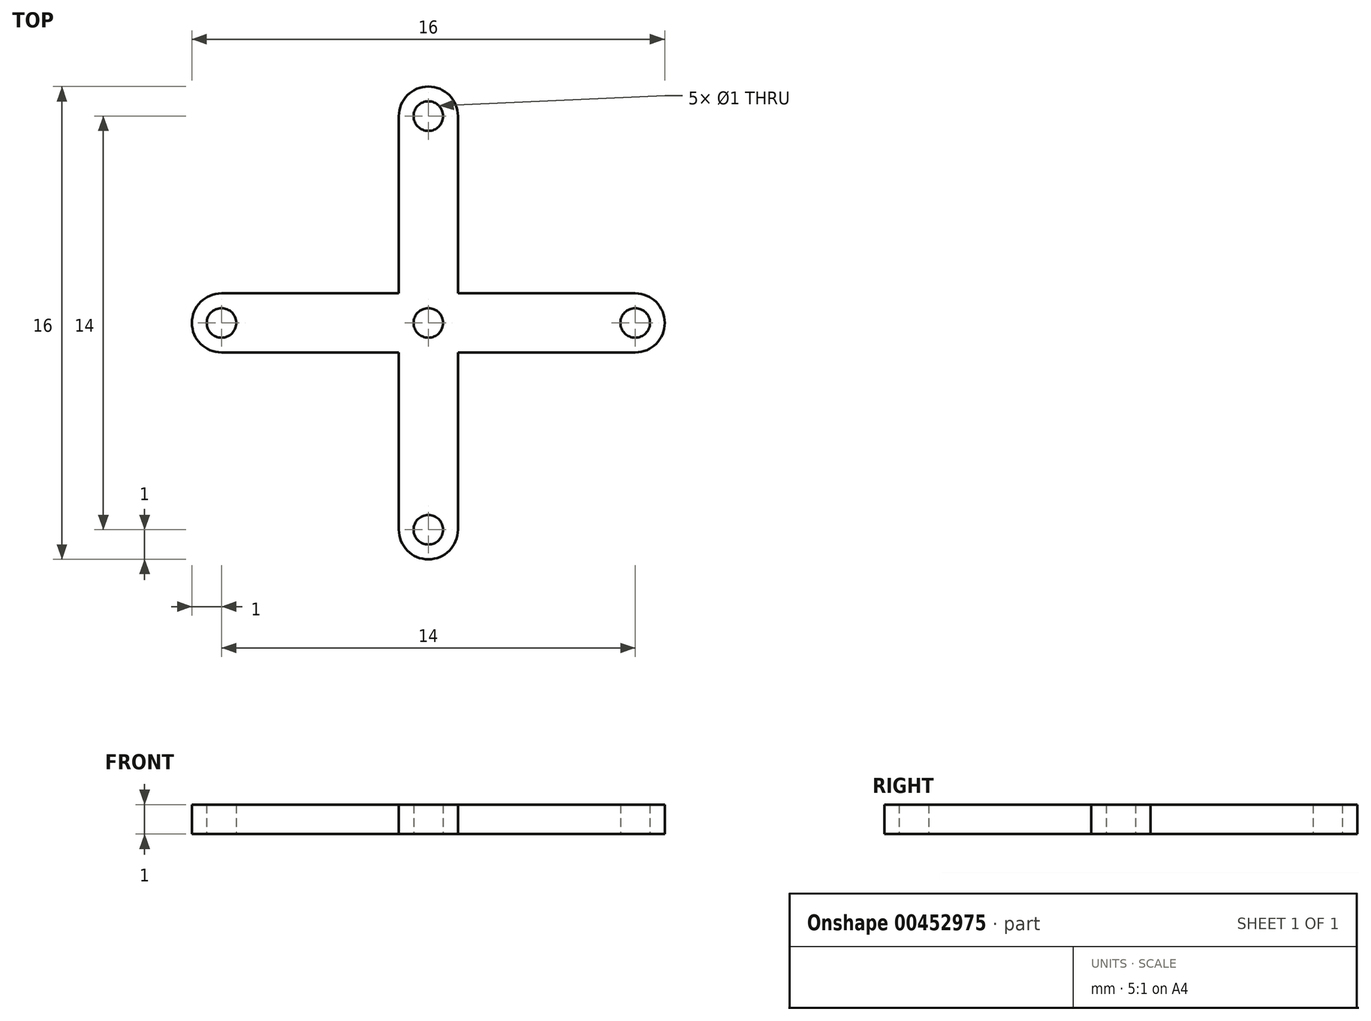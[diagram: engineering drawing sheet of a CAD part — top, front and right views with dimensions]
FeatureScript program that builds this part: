
annotation { "Feature Type Name" : "Feature", "Feature Type Description" : "" }
export const myFeature = defineFeature(function(context is Context, id is Id, definition is map)
    precondition{}
    {
        {
            var Q0;
            Q0=qCreatedBy(makeId("Top.planeOp"),FACE);
            var sketch = newSketch(context, id + "F0", { "sketchPlane" : qUnion([Q0])});
            skCircle(sketch, "E0", {"center": v(0, 7) * mm, "radius": 0.5 * mm});
            skCircle(sketch, "E1", {"center": v(0, 7) * mm, "radius": 1 * mm});
            skCircle(sketch, "E2.1.0", {"center": v(-7, 0) * mm, "radius": 0.5 * mm});
            skCircle(sketch, "E2.1.1", {"center": v(-7, 0) * mm, "radius": 1 * mm});
            skCircle(sketch, "E2.2.0", {"center": v(0, -7) * mm, "radius": 0.5 * mm});
            skCircle(sketch, "E2.2.1", {"center": v(0, -7) * mm, "radius": 1 * mm});
            skCircle(sketch, "E2.3.0", {"center": v(7, 0) * mm, "radius": 0.5 * mm});
            skCircle(sketch, "E2.3.1", {"center": v(7, 0) * mm, "radius": 1 * mm});
            skPoint(sketch, "E2.center", {"position": v(0, 0) * mm});
            skLineSegment(sketch, "E3", {"start": v(-1, 7) * mm, "end": v(-1, -7) * mm});
            skLineSegment(sketch, "E4.MirrorCS", {"start": v(1, 7) * mm, "end": v(1, -7) * mm});
            skLineSegment(sketch, "E5", {"start": v(-7, 1) * mm, "end": v(7, 1) * mm});
            skLineSegment(sketch, "E6.MirrorCS", {"start": v(-7, -1) * mm, "end": v(7, -1) * mm});
            skCircle(sketch, "E7", {"center": v(0, 0) * mm, "radius": 0.5 * mm});
            skSolve(sketch);
        }
        {
            var Q0;
            {var subQ0=sQuery(id+"F0.wireOp",EDGE,"E3");var subQ1=sQuery(id+"F0.wireOp",EDGE,"E1");var subQ2=makeQuery(id+"F0.imprint","INTERSECT",VERTEX,{"derivedFrom":[subQ1,subQ0]});Q0=makeQuery(id+"F0.imprint","IMPRINT",FACE,{"disambiguationData":[TD([[makeQuery(id+"F0.imprint","IMPRINT",EDGE,{"disambiguationData":[TD([[subQ2,-1.0]])],"derivedFrom":subQ1}),-1.0]])]});}
            var Q1;
            Q1=makeQuery(id+"F0.imprint","IMPRINT",FACE,{"disambiguationData":[TD([[makeQuery(id+"F0.imprint","IMPRINT",EDGE,{"derivedFrom":sQuery(id+"F0.wireOp",EDGE,"E7")}),-1.0]])]});
            var Q2;
            Q2=makeQuery(id+"F0.imprint","IMPRINT",FACE,{"disambiguationData":[TD([[makeQuery(id+"F0.imprint","IMPRINT",EDGE,{"derivedFrom":sQuery(id+"F0.wireOp",EDGE,"E0")}),-1.0]])]});
            var Q3;
            {var subQ0=sQuery(id+"F0.wireOp",EDGE,"E5");var subQ1=sQuery(id+"F0.wireOp",EDGE,"E2.3.1");var subQ2=makeQuery(id+"F0.imprint","INTERSECT",VERTEX,{"derivedFrom":[subQ1,subQ0]});Q3=makeQuery(id+"F0.imprint","IMPRINT",FACE,{"disambiguationData":[TD([[makeQuery(id+"F0.imprint","IMPRINT",EDGE,{"disambiguationData":[TD([[subQ2,-1.0]])],"derivedFrom":subQ1}),-1.0]])]});}
            var Q4;
            Q4=makeQuery(id+"F0.imprint","IMPRINT",FACE,{"disambiguationData":[TD([[makeQuery(id+"F0.imprint","IMPRINT",EDGE,{"derivedFrom":sQuery(id+"F0.wireOp",EDGE,"E2.3.0")}),-1.0]])]});
            var Q5;
            {var subQ0=sQuery(id+"F0.wireOp",EDGE,"E5");var subQ1=sQuery(id+"F0.wireOp",EDGE,"E2.1.1");var subQ2=makeQuery(id+"F0.imprint","INTERSECT",VERTEX,{"derivedFrom":[subQ1,subQ0]});Q5=makeQuery(id+"F0.imprint","IMPRINT",FACE,{"disambiguationData":[TD([[makeQuery(id+"F0.imprint","IMPRINT",EDGE,{"disambiguationData":[TD([[subQ2,1.0]])],"derivedFrom":subQ1}),-1.0]])]});}
            var Q6;
            Q6=makeQuery(id+"F0.imprint","IMPRINT",FACE,{"disambiguationData":[TD([[makeQuery(id+"F0.imprint","IMPRINT",EDGE,{"derivedFrom":sQuery(id+"F0.wireOp",EDGE,"E2.1.0")}),-1.0]])]});
            var Q7;
            {var subQ0=sQuery(id+"F0.wireOp",EDGE,"E3");var subQ1=sQuery(id+"F0.wireOp",EDGE,"E2.2.1");var subQ2=makeQuery(id+"F0.imprint","INTERSECT",VERTEX,{"derivedFrom":[subQ1,subQ0]});Q7=makeQuery(id+"F0.imprint","IMPRINT",FACE,{"disambiguationData":[TD([[makeQuery(id+"F0.imprint","IMPRINT",EDGE,{"disambiguationData":[TD([[subQ2,1.0]])],"derivedFrom":subQ1}),-1.0]])]});}
            var Q8;
            Q8=makeQuery(id+"F0.imprint","IMPRINT",FACE,{"disambiguationData":[TD([[makeQuery(id+"F0.imprint","IMPRINT",EDGE,{"derivedFrom":sQuery(id+"F0.wireOp",EDGE,"E2.2.0")}),-1.0]])]});
            extrude(context, id + "F1", {"entities" : qUnion([Q0, Q1, Q2, Q3, Q4, Q5, Q6, Q7, Q8]), "depth" : 1 * mm});
        }
    });
